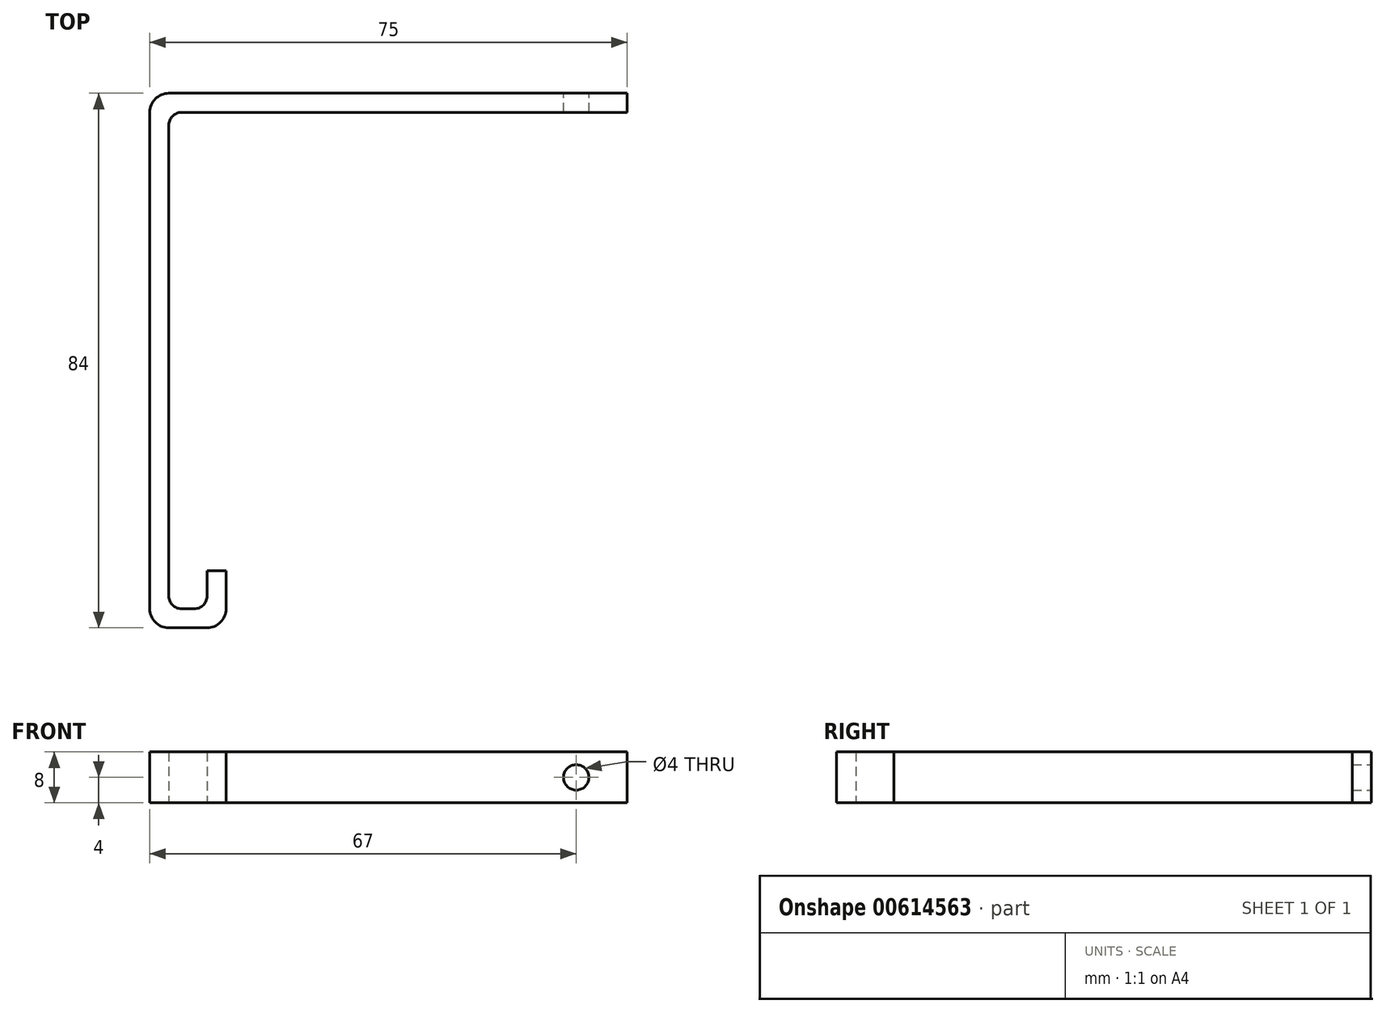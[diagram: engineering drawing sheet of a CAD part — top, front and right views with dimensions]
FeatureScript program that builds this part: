
annotation { "Feature Type Name" : "Feature", "Feature Type Description" : "" }
export const myFeature = defineFeature(function(context is Context, id is Id, definition is map)
    precondition{}
    {
        {
            var Q0;
            Q0=qCreatedBy(makeId("Top.planeOp"),FACE);
            var sketch = newSketch(context, id + "F0", { "sketchPlane" : qUnion([Q0])});
            skLineSegment(sketch, "E0", {"start": v(0, 0) * mm, "end": v(0, -78) * mm});
            skLineSegment(sketch, "E1", {"start": v(0, -78) * mm, "end": v(9, -78) * mm});
            skLineSegment(sketch, "E2", {"start": v(9, -78) * mm, "end": v(9, -81) * mm});
            skLineSegment(sketch, "E3", {"start": v(9, -81) * mm, "end": v(-3, -81) * mm});
            skLineSegment(sketch, "E4", {"start": v(-3, -81) * mm, "end": v(-3, 3) * mm});
            skLineSegment(sketch, "E5", {"start": v(-3, 3) * mm, "end": v(72, 3) * mm});
            skLineSegment(sketch, "E6", {"start": v(72, 3) * mm, "end": v(72, 0) * mm});
            skLineSegment(sketch, "E7", {"start": v(72, 0) * mm, "end": v(0, 0) * mm});
            skLineSegment(sketch, "E8", {"start": v(9, -78) * mm, "end": v(9, -72) * mm});
            skLineSegment(sketch, "E9", {"start": v(9, -72) * mm, "end": v(6, -72) * mm});
            skLineSegment(sketch, "E10", {"start": v(6, -72) * mm, "end": v(6, -78) * mm});
            skSolve(sketch);
        }
        {
            var Q0;
            Q0 = qSketchRegion(id + "F0", true);
            extrude(context, id + "F1", {"entities" : qUnion([Q0]), "depth" : 8 * mm, "offsetDistance" : 25 * mm});
        }
        {
            var Q0;
            Q0=makeQuery(id+"F1.opExtrude","SWEPT_FACE",FACE,{"disambiguationData":[OSD([sQuery(id+"F0.wireOp",EDGE,"E5")])]});
            var sketch = newSketch(context, id + "F2", { "sketchPlane" : qUnion([Q0])});
            skLineSegment(sketch, "E11", {"start": v(-72, 4) * mm, "end": v(-64, 4) * mm});
            skSolve(sketch);
        }
        {
            var Q0;
            Q0=sQuery(id+"F2.wireOp",VERTEX,"E11.end");
            var Q1;
            Q1=makeQuery(id+"F1.opExtrude","SWEPT_BODY",BODY,{"disambiguationData":[OSD([sQuery(id+"F0.wireOp",EDGE,"E0"),sQuery(id+"F0.wireOp",EDGE,"E1"),sQuery(id+"F0.wireOp",EDGE,"E2"),sQuery(id+"F0.wireOp",EDGE,"E3"),sQuery(id+"F0.wireOp",EDGE,"E4"),sQuery(id+"F0.wireOp",EDGE,"E5"),sQuery(id+"F0.wireOp",EDGE,"E6"),sQuery(id+"F0.wireOp",EDGE,"E7")])]});
            hole(context, id + "F3", {"style" : HoleStyle.SIMPLE, "endStyle" : HoleEndStyle.BLIND, "holeDiameter" : 4 * mm, "majorDiameter" : 5 * mm, "holeDepth" : 10 * mm, "isTappedThrough" : true, "tappedDepth" : 12 * mm, "tapClearance" : 3, "locations" : qUnion([Q0]), "scope" : qUnion([Q1])});
        }
        {
            var Q0;
            Q0=makeQuery(id+"F1.opExtrude","SWEPT_EDGE",EDGE,{"disambiguationData":[OSD([sQuery(id+"F0.wireOp",EDGE,"E3"),sQuery(id+"F0.wireOp",EDGE,"E4")])]});
            var Q1;
            Q1=makeQuery(id+"F1.opExtrude","SWEPT_EDGE",EDGE,{"disambiguationData":[OSD([sQuery(id+"F0.wireOp",EDGE,"E4"),sQuery(id+"F0.wireOp",EDGE,"E5")])]});
            var Q2;
            Q2=makeQuery(id+"F1.opExtrude","SWEPT_EDGE",EDGE,{"disambiguationData":[OSD([sQuery(id+"F0.wireOp",EDGE,"E2"),sQuery(id+"F0.wireOp",EDGE,"E3")])]});
            fillet(context, id + "F4", {"entities" : qUnion([Q0, Q1, Q2]), "radius" : 3 * mm, "tangentPropagation" : true, "allowEdgeOverflow" : false});
        }
        {
            var Q0;
            Q0=makeQuery(id+"F1.opExtrude","SWEPT_EDGE",EDGE,{"disambiguationData":[OSD([sQuery(id+"F0.wireOp",EDGE,"E1"),sQuery(id+"F0.wireOp",EDGE,"E10")])]});
            var Q1;
            Q1=makeQuery(id+"F1.opExtrude","SWEPT_EDGE",EDGE,{"disambiguationData":[OSD([sQuery(id+"F0.wireOp",EDGE,"E0"),sQuery(id+"F0.wireOp",EDGE,"E1")])]});
            var Q2;
            Q2=makeQuery(id+"F1.opExtrude","SWEPT_EDGE",EDGE,{"disambiguationData":[OSD([sQuery(id+"F0.wireOp",EDGE,"E0"),sQuery(id+"F0.wireOp",EDGE,"E7")])]});
            fillet(context, id + "F5", {"entities" : qUnion([Q0, Q1, Q2]), "radius" : 2 * mm, "tangentPropagation" : true, "allowEdgeOverflow" : false});
        }
    });
